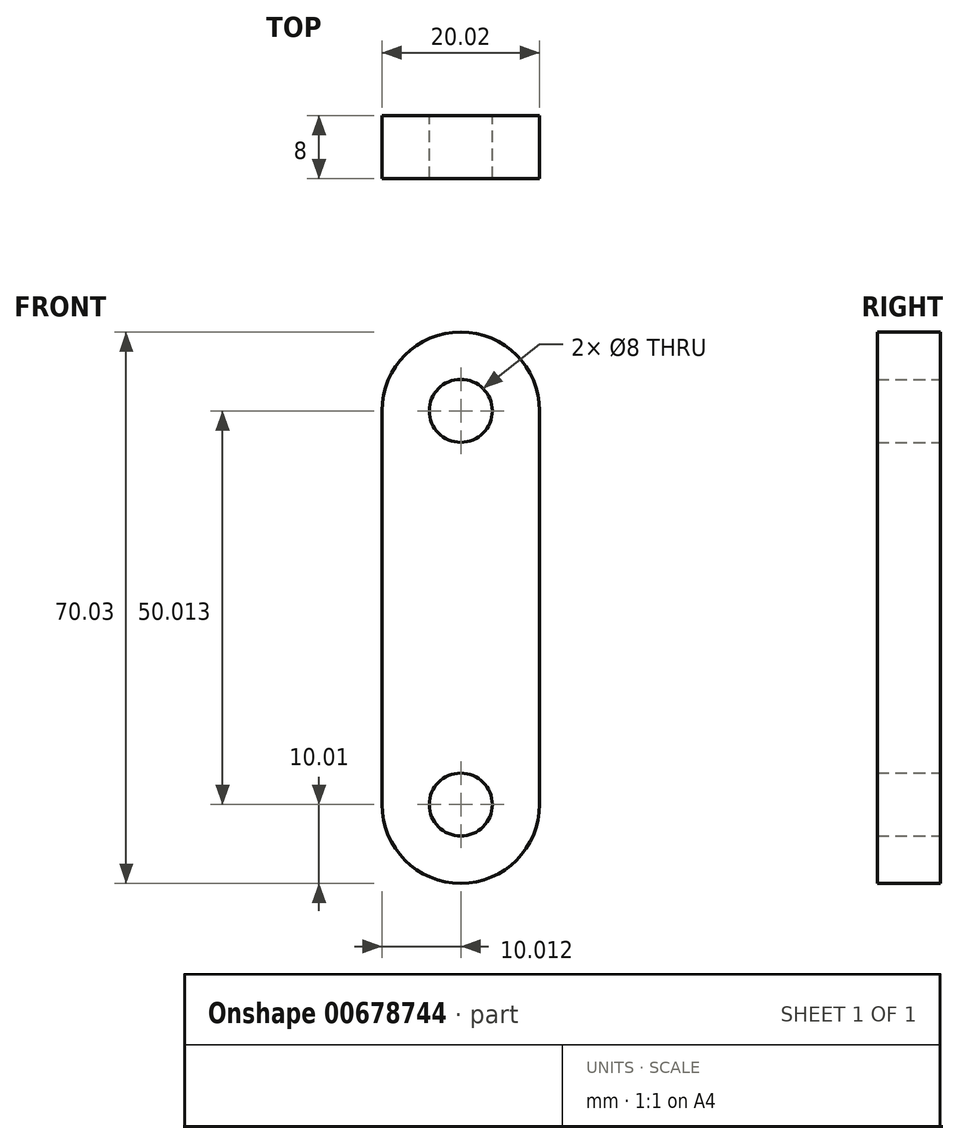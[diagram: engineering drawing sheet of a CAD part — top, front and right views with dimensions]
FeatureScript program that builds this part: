
annotation { "Feature Type Name" : "Feature", "Feature Type Description" : "" }
export const myFeature = defineFeature(function(context is Context, id is Id, definition is map)
    precondition{}
    {
        {
            var Q0;
            Q0=qCreatedBy(makeId("Front.planeOp"),FACE);
            var sketch = newSketch(context, id + "F0", { "sketchPlane" : qUnion([Q0])});
            skLineSegment(sketch, "E0.bottom", {"start": v(-20.02, 50.01) * mm, "end": v(0, 50.01) * mm});
            skLineSegment(sketch, "E0.top", {"start": v(-20.02, 0) * mm, "end": v(0, 0) * mm});
            skLineSegment(sketch, "E0.left", {"start": v(-20.02, 50.01) * mm, "end": v(-20.02, 0) * mm});
            skLineSegment(sketch, "E0.right", {"start": v(0, 50.01) * mm, "end": v(0, 0) * mm});
            skCircle(sketch, "E1", {"center": v(-10, 50.01) * mm, "radius": 10 * mm});
            skCircle(sketch, "E2", {"center": v(-10, 0) * mm, "radius": 10 * mm});
            skCircle(sketch, "E3", {"center": v(-10, 50.01) * mm, "radius": 4 * mm});
            skCircle(sketch, "E4", {"center": v(-10, 0) * mm, "radius": 4 * mm});
            skSolve(sketch);
        }
        {
            var Q0;
            {var subQ1=sQuery(id+"F0.wireOp",EDGE,"E0.bottom");var subQ3=sQuery(id+"F0.wireOp",EDGE,"E3");var subQ4=makeQuery(id+"F0.imprint","INTERSECT",VERTEX,{"disambiguationData":[OD(0.0)],"derivedFrom":[subQ1,subQ3]});Q0=makeQuery(id+"F0.imprint","IMPRINT",FACE,{"disambiguationData":[TD([[makeQuery(id+"F0.imprint","IMPRINT",EDGE,{"disambiguationData":[TD([[subQ4,1.0]])],"derivedFrom":subQ3}),-1.0]])]});}
            var Q1;
            {var subQ1=sQuery(id+"F0.wireOp",EDGE,"E0.bottom");var subQ3=sQuery(id+"F0.wireOp",EDGE,"E3");var subQ4=makeQuery(id+"F0.imprint","INTERSECT",VERTEX,{"disambiguationData":[OD(0.0)],"derivedFrom":[subQ1,subQ3]});Q1=makeQuery(id+"F0.imprint","IMPRINT",FACE,{"disambiguationData":[TD([[makeQuery(id+"F0.imprint","IMPRINT",EDGE,{"disambiguationData":[TD([[subQ4,-1.0]])],"derivedFrom":subQ3}),-1.0]])]});}
            var Q2;
            {var subQ0=sQuery(id+"F0.wireOp",EDGE,"E0.left");Q2=makeQuery(id+"F0.imprint","IMPRINT",FACE,{"disambiguationData":[TD([[makeQuery(id+"F0.imprint","IMPRINT",EDGE,{"derivedFrom":subQ0}),1.0]])]});}
            var Q3;
            {var subQ1=sQuery(id+"F0.wireOp",EDGE,"E0.top");var subQ3=sQuery(id+"F0.wireOp",EDGE,"E4");var subQ4=makeQuery(id+"F0.imprint","INTERSECT",VERTEX,{"disambiguationData":[OD(0.0)],"derivedFrom":[subQ1,subQ3]});Q3=makeQuery(id+"F0.imprint","IMPRINT",FACE,{"disambiguationData":[TD([[makeQuery(id+"F0.imprint","IMPRINT",EDGE,{"disambiguationData":[TD([[subQ4,1.0]])],"derivedFrom":subQ3}),-1.0]])]});}
            var Q4;
            {var subQ1=sQuery(id+"F0.wireOp",EDGE,"E0.top");var subQ3=sQuery(id+"F0.wireOp",EDGE,"E4");var subQ4=makeQuery(id+"F0.imprint","INTERSECT",VERTEX,{"disambiguationData":[OD(0.0)],"derivedFrom":[subQ1,subQ3]});Q4=makeQuery(id+"F0.imprint","IMPRINT",FACE,{"disambiguationData":[TD([[makeQuery(id+"F0.imprint","IMPRINT",EDGE,{"disambiguationData":[TD([[subQ4,-1.0]])],"derivedFrom":subQ3}),-1.0]])]});}
            extrude(context, id + "F1", {"entities" : qUnion([Q0, Q1, Q2, Q3, Q4]), "depth" : 8 * mm, "offsetDistance" : 25 * mm});
        }
    });
